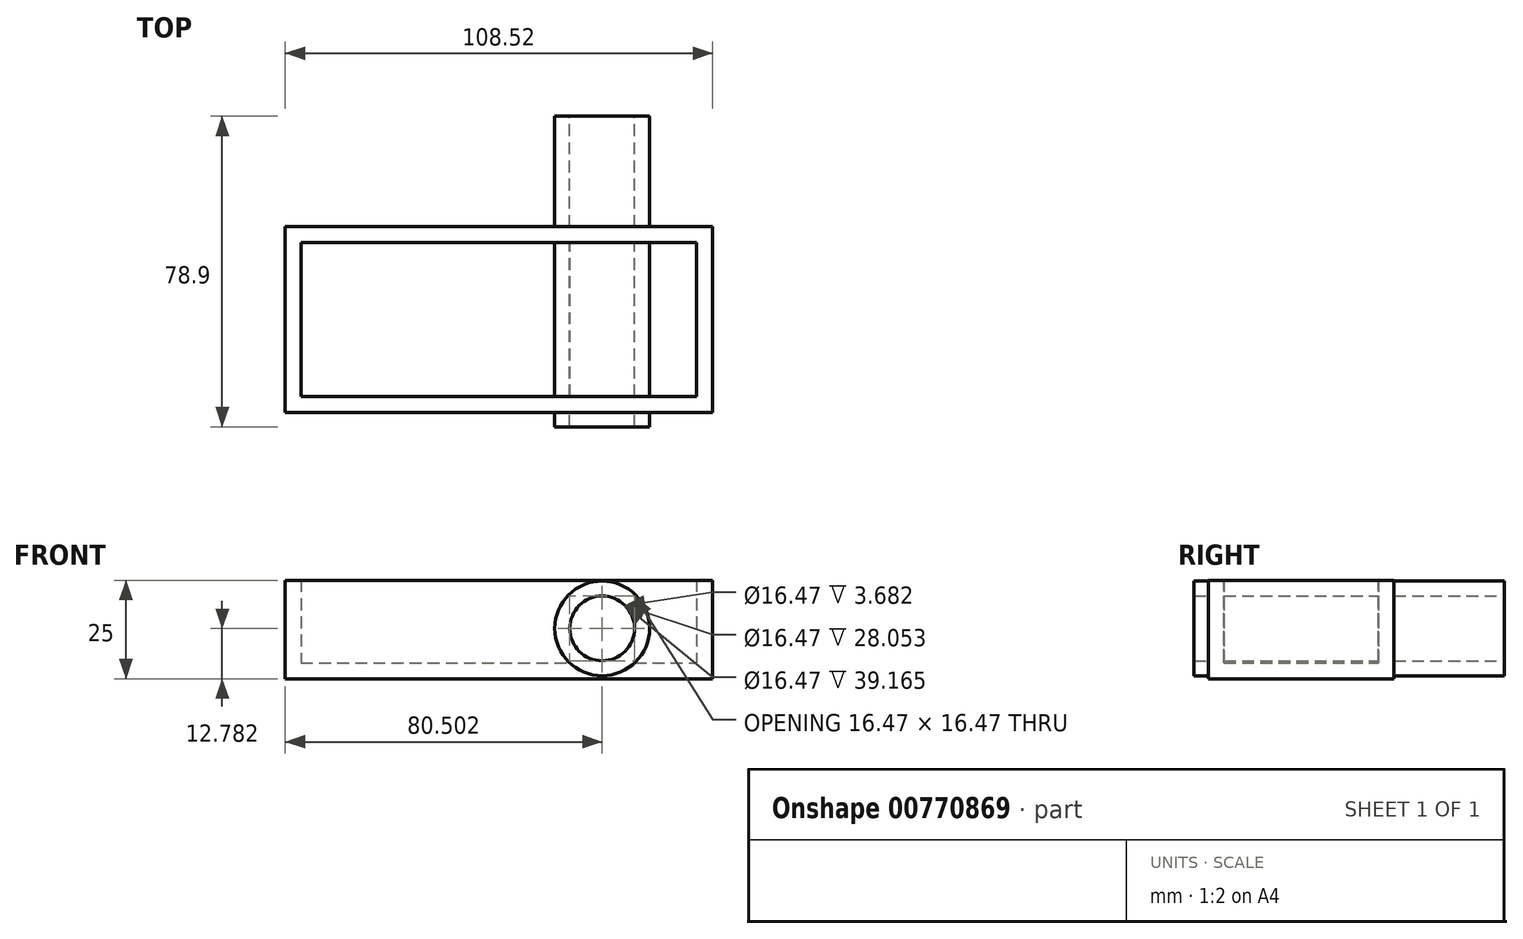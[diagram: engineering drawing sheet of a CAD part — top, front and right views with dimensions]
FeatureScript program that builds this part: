
annotation { "Feature Type Name" : "Feature", "Feature Type Description" : "" }
export const myFeature = defineFeature(function(context is Context, id is Id, definition is map)
    precondition{}
    {
        {
            var Q0;
            Q0=qCreatedBy(makeId("Top.planeOp"),FACE);
            var sketch = newSketch(context, id + "F0", { "sketchPlane" : qUnion([Q0])});
            skLineSegment(sketch, "E0.bottom", {"start": v(-44.14, 20.85) * mm, "end": v(64.38, 20.85) * mm});
            skLineSegment(sketch, "E0.top", {"start": v(-44.14, -26.32) * mm, "end": v(64.38, -26.32) * mm});
            skLineSegment(sketch, "E0.left", {"start": v(-44.14, 20.85) * mm, "end": v(-44.14, -26.32) * mm});
            skLineSegment(sketch, "E0.right", {"start": v(64.38, 20.85) * mm, "end": v(64.38, -26.32) * mm});
            skSolve(sketch);
        }
        {
            var Q0;
            Q0 = qSketchRegion(id + "F0", true);
            extrude(context, id + "F1", {"entities" : qUnion([Q0]), "depth" : 25 * mm, "offsetDistance" : 25 * mm});
        }
        {
            var Q0;
            Q0=makeQuery(id+"F1.opExtrude","CAP_FACE",FACE,{"disambiguationData":[OSD([sQuery(id+"F0.wireOp",EDGE,"E0.bottom"),sQuery(id+"F0.wireOp",EDGE,"E0.top"),sQuery(id+"F0.wireOp",EDGE,"E0.left"),sQuery(id+"F0.wireOp",EDGE,"E0.right")])],"isStart":false});
            shell(context, id + "F2", {"entities" : qUnion([Q0]), "thickness" : 4 * mm});
        }
        {
            var Q0;
            Q0=qCreatedBy(makeId("Front.planeOp"),FACE);
            var sketch = newSketch(context, id + "F3", { "sketchPlane" : qUnion([Q0])});
            skCircle(sketch, "E1", {"center": v(36.36, 12.78) * mm, "radius": 12.03 * mm});
            skCircle(sketch, "E2", {"center": v(36.36, 12.78) * mm, "radius": 8.23 * mm});
            skSolve(sketch);
        }
        {
            var Q0;
            Q0 = qSketchRegion(id + "F3", true);
            extrude(context, id + "F4", {"entities" : qUnion([Q0]), "depth" : 30 * mm, "offsetDistance" : 25 * mm, "hasSecondDirection" : true, "secondDirectionOppositeDirection" : true, "secondDirectionDepth" : 30 * mm});
        }
        {
            var Q0;
            Q0=makeQuery(id+"F4.opExtrude","CAP_FACE",FACE,{"disambiguationData":[OSD([sQuery(id+"F3.wireOp",EDGE,"E1"),sQuery(id+"F3.wireOp",EDGE,"E2")])],"isStart":false});
            extrude(context, id + "F5", {"entities" : qUnion([Q0]), "operationType" : NewBodyOperationType.ADD, "oppositeDirection" : true, "depth" : 78.9 * mm, "offsetDistance" : 25 * mm});
        }
    });
